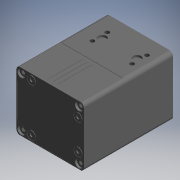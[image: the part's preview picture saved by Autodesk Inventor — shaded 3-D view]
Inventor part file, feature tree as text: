
AUTODESK INVENTOR PART (.ipt)
format: ipt  version: 2017.3 (Build 213256000, 256)  size: 654,336 bytes
history: native  units: mm (DEFAULTED — no unit token found)
features: other x42, sketch x30, revolve x21, extrude x17, pattern_linear x13, hole x6
ambient origin geometry x8: Origin, YZ Plane, XZ Plane, XY Plane, X Axis, Y Axis, Z Axis, Center Point
bodies: Solid1 (feature_tree)
feature tree (129):
  extrude  "Extrusion1"  Depth=42.0mm TaperAngle=0.0deg
  extrude  "Extrusion2"  Depth=2.5mm TaperAngle=0.0deg
  extrude  "Extrusion3"  Depth=2.5mm TaperAngle=0.0deg
  extrude  "Extrusion4"  Depth=2.5mm TaperAngle=0.0deg
  other  "Aussparung_1_SKETCH_1"
  other  "Aussparung_1_SKETCH_2"
  extrude  "Extrusion5"  Depth=2.5mm TaperAngle=0.0deg
  extrude  "Extrusion6"  Depth=90.0mm
  extrude  "Extrusion7"  Depth=90.0mm
  other  "Aussparung_2_SKETCH_1"
  other  "Aussparung_2_SKETCH_2"
  extrude  "Extrusion8"  Depth=90.0mm
  extrude  "Extrusion9"  Depth=20.0mm
  extrude  "Extrusion10"  Depth=20.0mm
  revolve  "Revolution1"  [1 undecoded]
  pattern_linear  "Rectangular Pattern1"  Count1=2 Spacing1=35.0mm
  revolve  "Revolution2"  [1 undecoded]
  pattern_linear  "Rectangular Pattern2"  Count1=2 Spacing1=15.0mm
  extrude  "Extrusion11"  Depth=20.0mm
  pattern_linear  "Rectangular Pattern3"  Count1=2 Spacing1=10.0mm
  hole  "Hole1"  [1 undecoded]
  pattern_linear  "Rectangular Pattern4"  Count1=2 Spacing1=10.0mm
  hole  "Hole2"  [1 undecoded]
  pattern_linear  "Rectangular Pattern5"  Spacing1=360.0deg  [1 undecoded]
  hole  "Hole3"  [1 undecoded]
  pattern_linear  "Rectangular Pattern6"  Spacing1=360.0deg  [1 undecoded]
  revolve  "Revolution3"  Angle=360.0deg
  pattern_linear  "Rectangular Pattern7"  Spacing1=360.0deg  [1 undecoded]
  hole  "Hole4"  [1 undecoded]
  pattern_linear  "Rectangular Pattern8"  Spacing1=360.0deg  [1 undecoded]
  extrude  "Extrusion12"  TaperAngle=360.0deg  [1 undecoded]
  hole  "Hole5"  [1 undecoded]
  revolve  "Revolution4"  [1 undecoded]
  pattern_linear  "Rectangular Pattern9"  Spacing1=0.0mm  [1 undecoded]
  extrude  "Extrusion13"  [1 undecoded]
  pattern_linear  "Rectangular Pattern10"  [2 undecoded]
  revolve  "Revolution5"  [1 undecoded]
  extrude  "Extrusion14"  [1 undecoded]
  hole  "Hole6"  [1 undecoded]
  sketch  "Sketch_32"  dims[d135=360.0deg d136=20.0mm d138=20.0mm d139=10.0mm d141=0.0mm]
  revolve  "Revolution6"  [1 undecoded]
  pattern_linear  "Rectangular Pattern11"  [2 undecoded]
  revolve  "Revolution7"  [1 undecoded]
  pattern_linear  "Rectangular Pattern12"  [2 undecoded]
  extrude  "Extrusion15"  [1 undecoded]
  pattern_linear  "Rectangular Pattern13"  [2 undecoded]
  extrude  "Extrusion16"  [1 undecoded]
  revolve  "Revolution8"  [1 undecoded]
  revolve  "Revolution9"  [1 undecoded]
  other  "Stecker_SKETCH_1"
  other  "Stecker_SKETCH_2"
  other  "Stecker_SKETCH_3"
  revolve  "Revolution10"  [1 undecoded]
  revolve  "Revolution11"  [1 undecoded]
  revolve  "Revolution12"  [1 undecoded]
  revolve  "Revolution13"  [1 undecoded]
  extrude  "Extrusion17"  [1 undecoded]
  revolve  "Revolution14"  [1 undecoded]
  other  "Stecker_2_3_SKETCH_1"
  other  "Stecker_2_3_SKETCH_2"
  other  "Stecker_2_3_SKETCH_3"
  other  "Stecker_2_3_SKETCH_4"
  other  "Stecker_2_3_SKETCH_5"
  other  "Stecker_2_3_SKETCH_6"
  other  "Stecker_2_3_SKETCH_7"
  revolve  "Revolution15"  [1 undecoded]
  revolve  "Revolution16"  [1 undecoded]
  revolve  "Revolution17"  [1 undecoded]
  revolve  "Revolution18"  [1 undecoded]
  revolve  "Revolution19"  [1 undecoded]
  revolve  "Revolution20"  [1 undecoded]
  revolve  "Revolution21"  [1 undecoded]
  other  "dec_XY"
  other  "dec_YZ"
  other  "dec_ZX"
  other  "dec_X"
  other  "dec_Y"
  other  "dec_Z"
  other  "dec_Center"
  other  "dummy_XY"
  other  "dummy_YZ"
  other  "dummy_ZX"
  other  "dummy_X"
  other  "dummy_Y"
  other  "dummy_Z"
  other  "dummy_Center"
  other  "klemmh_XY"
  other  "klemmh_YZ"
  other  "klemmh_ZX"
  other  "klemmh_X"
  other  "klemmh_Y"
  other  "klemmh_Z"
  other  "klemmh_Center"
  other  "stk_XY"
  other  "stk_YZ"
  other  "stk_ZX"
  other  "stk_X"
  other  "stk_Y"
  other  "stk_Z"
  other  "stk_Center"
  sketch  "Sketch_1"  dims[d0=90.0mm d1=0.0mm d2=42.0mm d3=0.0mm]
  sketch  "Sketch_5"  dims[d12=2.5mm d13=0.0mm d14=2.5mm d15=0.0mm]
  sketch  "Sketch_6"  dims[d16=2.5mm d17=0.0mm d18=0.1mm d19=0.0mm]
  sketch  "Sketch_2"  dims[d4=42.0mm d5=0.0mm d6=2.5mm d7=0.0mm]
  sketch  "Sketch_4"  dims[d8=2.5mm d9=0.0mm d10=2.5mm d11=0.0mm]
  sketch  "Sketch_8"  dims[d20=360.0deg d21=90.0mm d23=6.0mm d24=20.0mm d26=47.853944mm]
  sketch  "Sketch_45"  dims[d162=360.0deg]
  sketch  "Sketch_46"  dims[d163=360.0deg]
  sketch  "Sketch_49"  dims[d164=360.0deg]
  sketch  "Sketch14"  dims[d42=4.134mm d43=18.1mm d44=8.0mm d45=2.1mm d46=90.0deg d47=18.1mm d48=20.594885mm d49=20.0mm d51=58.0mm d52=20.0mm d54=50.0mm]
  sketch  "Sketch15"  dims[d55=4.134mm d56=9.0mm d57=4.0mm d58=2.0mm d59=90.0deg d60=12.0mm d61=120.0deg d62=20.0mm d64=40.0mm d65=20.0mm d67=15.0mm]
  sketch  "Sketch16"  dims[d68=4.134mm d69=9.0mm d70=4.0mm d71=2.0mm d72=90.0deg d73=12.0mm d74=120.0deg d75=20.0mm d77=40.0mm d78=20.0mm d80=15.0mm]
  sketch  "Sketch_19"  dims[d88=8.0mm d89=6.0mm d90=4.0mm d91=2.0mm d92=90.0deg d93=2.1mm d94=0.0mm d95=20.0mm d97=35.0mm d98=10.0mm d100=0.0mm]
  sketch  "Sketch18"  dims[d81=360.0deg d82=20.0mm d84=35.0mm d85=10.0mm d87=0.0mm]
  sketch  "Sketch_23"  dims[d103=8.2mm d104=6.0mm d105=4.0mm d106=2.0mm d107=90.0deg d108=2.0mm d109=0.0mm]
  sketch  "Sketch20"  dims[d101=1.5mm d102=0.0mm]
  sketch  "Sketch_25"  dims[d110=360.0deg d111=20.0mm d113=15.0mm d114=20.0mm d116=15.0mm]
  sketch  "Sketch_27"  dims[d125=360.0deg]
  sketch  "Sketch_29"  dims[d126=1.6mm d127=0.0mm]
  sketch  "Sketch_30"  dims[d128=4.0mm d129=6.0mm d130=4.0mm d131=2.0mm d132=90.0deg d133=2.0mm d134=0.0mm]
  sketch  "Sketch25"  dims[d117=1.0mm d118=0.0mm d119=20.0mm d121=15.0mm d122=20.0mm d124=15.0mm]
  sketch  "Sketch_11"  dims[d34=1.0mm d35=0.0mm d36=90.0mm d38=6.0mm d39=20.0mm d41=47.853944mm]
  sketch  "Sketch_51"  dims[d165=9.0mm d166=0.0mm d167=360.0deg d168=360.0deg d169=360.0deg d170=360.0deg d171=360.0deg d172=360.0deg d173=360.0deg d174=360.0deg d175=0.0mm d176=0.0mm d177=0.0mm]
  sketch  "Sketch_35"  dims[d142=360.0deg d143=20.0mm d145=20.0mm d146=10.0mm d148=0.0mm]
  sketch  "Sketch_39"  dims[d157=2.0mm d158=0.0mm d159=360.0deg]
  sketch  "Sketch_10"  dims[d27=360.0deg d28=90.0mm d30=6.0mm d31=20.0mm d33=47.853944mm]
  sketch  "Sketch_38"  dims[d149=1.3mm d150=0.0mm d151=20.0mm d153=20.0mm d154=10.0mm d156=0.0mm]
  sketch  "Sketch_42"  dims[d160=360.0deg]
  sketch  "Sketch_43"  dims[d161=360.0deg]
note: 45 required parameter values undecoded (feature->parameter linkage not recoverable at this tier; creation-order binding heuristic only, values carry confidence <= 0.55)